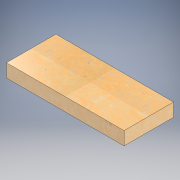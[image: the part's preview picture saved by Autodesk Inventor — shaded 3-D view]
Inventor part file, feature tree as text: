
AUTODESK INVENTOR PART (.ipt)
format: ipt  version: 2022.2 (Build 262287010, 287A)  size: 131,584 bytes
history: native  units: in
note: dims shown in document units (in); Inventor stores cm internally (conversion verified against a paired STEP export)
features: extrude x1, sketch x1
ambient origin geometry x8: Origin, YZ Plane, XZ Plane, XY Plane, X Axis, Y Axis, Z Axis, Center Point
bodies: Solid1 (feature_tree)
feature tree (2):
  extrude  "Extrusion1"  Depth=15.0in
  sketch  "Sketch1"  dims[d0=35.625in d1=15.0in d2=4.0in d3=0.0in]
